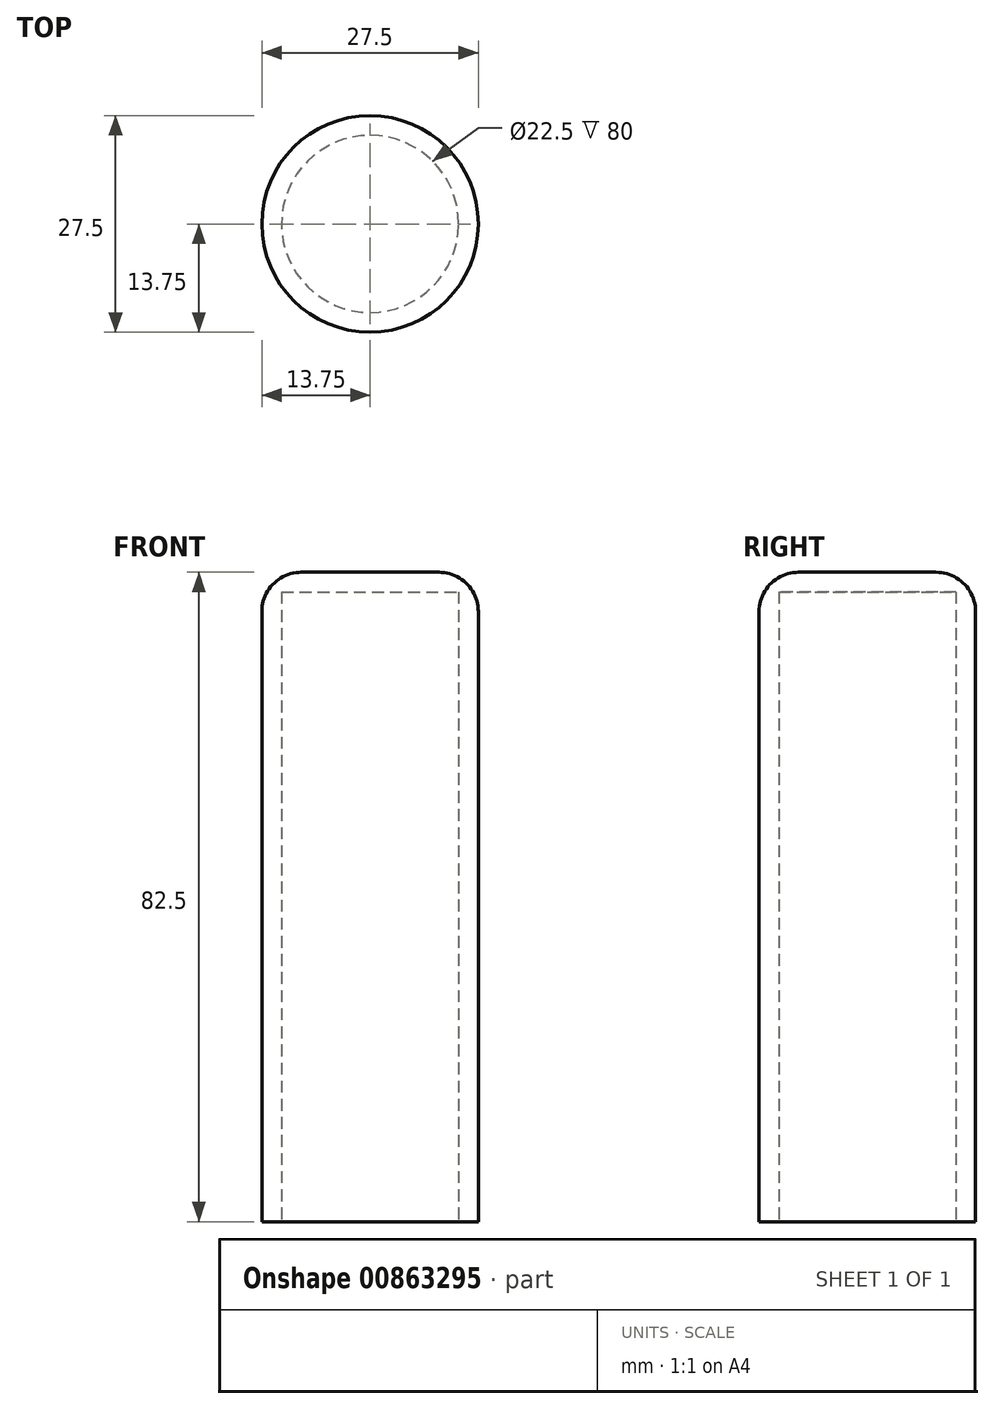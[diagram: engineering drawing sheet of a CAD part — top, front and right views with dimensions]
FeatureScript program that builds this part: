
annotation { "Feature Type Name" : "Feature", "Feature Type Description" : "" }
export const myFeature = defineFeature(function(context is Context, id is Id, definition is map)
    precondition{}
    {
        {
            var Q0;
            Q0=qCreatedBy(makeId("Front.planeOp"),FACE);
            var sketch = newSketch(context, id + "F0", { "sketchPlane" : qUnion([Q0])});
            skLineSegment(sketch, "E0", {"start": v(0, 0) * mm, "end": v(0, 82.5) * mm});
            skLineSegment(sketch, "E1", {"start": v(0, 82.5) * mm, "end": v(8.75, 82.5) * mm});
            skLineSegment(sketch, "E2", {"start": v(13.75, 77.5) * mm, "end": v(13.75, 0) * mm});
            skLineSegment(sketch, "E3", {"start": v(13.75, 0) * mm, "end": v(11.25, 0) * mm});
            skLineSegment(sketch, "E4", {"start": v(11.25, 0) * mm, "end": v(11.25, 80) * mm});
            skLineSegment(sketch, "E5", {"start": v(11.25, 80) * mm, "end": v(0, 80) * mm});
            skPoint(sketch, "E6.visualSharp", {"position": v(13.75, 82.5) * mm});
            skArc(sketch, "E6.filletArc", {"start": v(13.75, 77.5) * mm, "mid": v(12.29, 81.04) * mm, "end": v(8.75, 82.5) * mm});
            skSolve(sketch);
        }
        {
            var Q0;
            Q0=qSketchRegion(id+"F0",true);
            var Q1;
            Q1=sQuery(id+"F0.wireOp",EDGE,"E0");
            revolve(context, id + "F1", {"surfaceOperationType" : NewSurfaceOperationType.NEW, "entities" : qUnion([Q0]), "axis" : qUnion([Q1]), "revolveType" : RevolveType.FULL});
        }
    });
